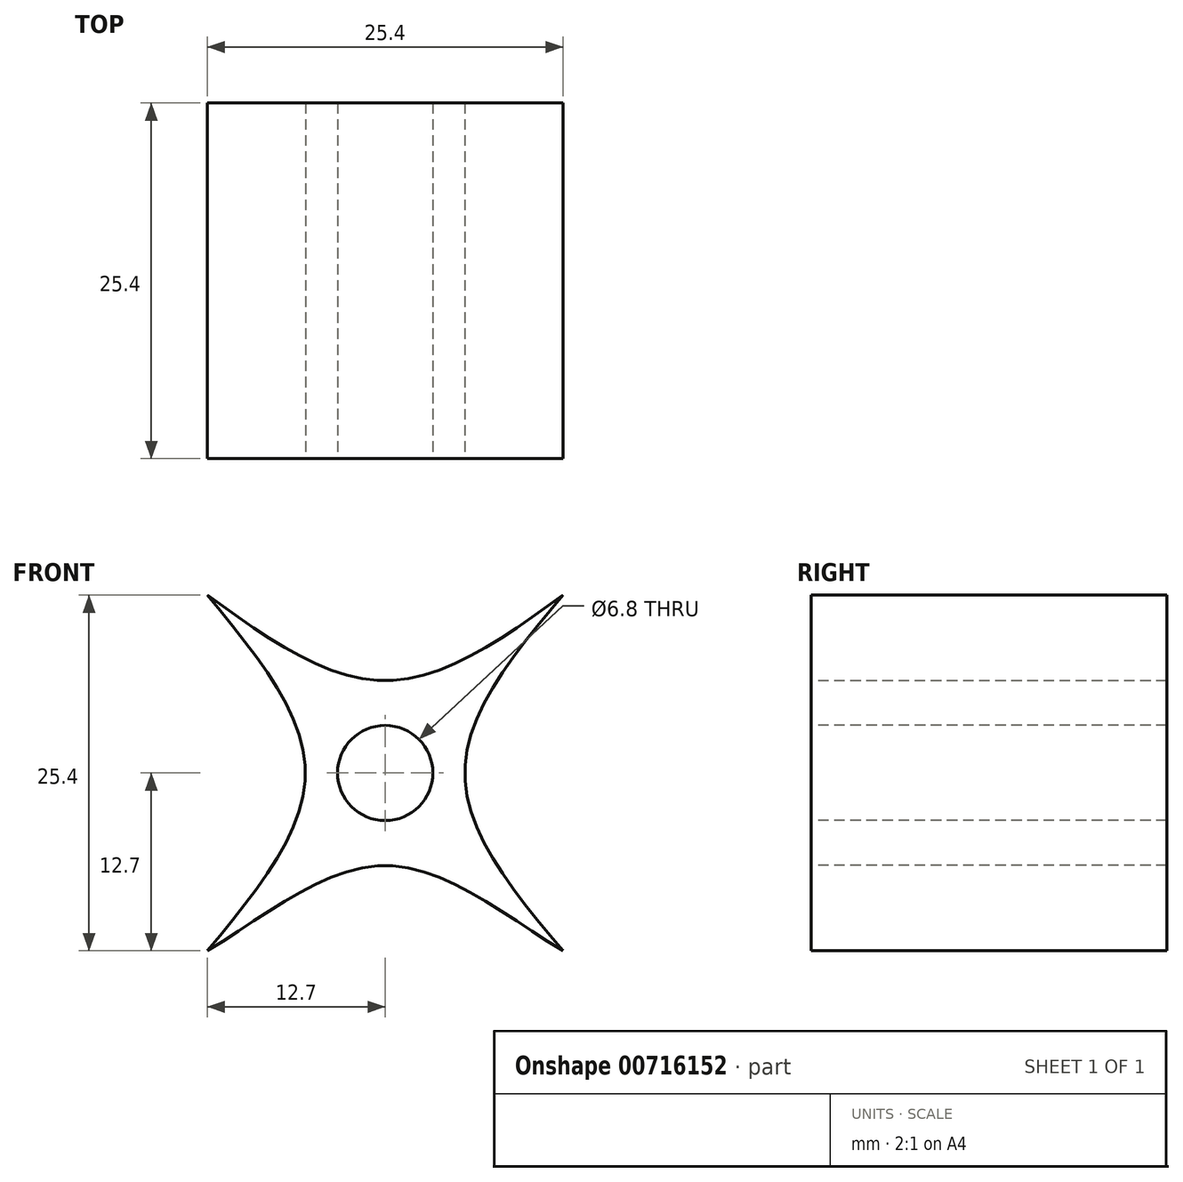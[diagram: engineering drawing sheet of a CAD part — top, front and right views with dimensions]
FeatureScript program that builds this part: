
annotation { "Feature Type Name" : "Feature", "Feature Type Description" : "" }
export const myFeature = defineFeature(function(context is Context, id is Id, definition is map)
    precondition{}
    {
        {
            var Q0;
            Q0=qCreatedBy(makeId("Front.planeOp"),FACE);
            var sketch = newSketch(context, id + "F0", { "sketchPlane" : qUnion([Q0])});
            skLineSegment(sketch, "E0.bottom", {"start": v(12.7, 12.7) * mm, "end": v(-12.7, 12.7) * mm});
            skLineSegment(sketch, "E0.top", {"start": v(12.7, -12.7) * mm, "end": v(-12.7, -12.7) * mm});
            skLineSegment(sketch, "E0.left", {"start": v(12.7, 12.7) * mm, "end": v(12.7, -12.7) * mm});
            skLineSegment(sketch, "E0.right", {"start": v(-12.7, 12.7) * mm, "end": v(-12.7, -12.7) * mm});
            skPoint(sketch, "E0.middle", {"position": v(0, 0) * mm});
            skSolve(sketch);
        }
        {
            var Q0;
            Q0 = qSketchRegion(id + "F0", true);
            extrude(context, id + "F1", {"entities" : qUnion([Q0]), "depth" : 25.4 * mm, "offsetDistance" : 25.4 * mm});
        }
        {
            var Q0;
            Q0=makeQuery(id+"F1.opExtrude","CAP_FACE",FACE,{"disambiguationData":[OSD([sQuery(id+"F0.wireOp",EDGE,"E0.bottom"),sQuery(id+"F0.wireOp",EDGE,"E0.top"),sQuery(id+"F0.wireOp",EDGE,"E0.left"),sQuery(id+"F0.wireOp",EDGE,"E0.right")])],"isStart":false});
            var sketch = newSketch(context, id + "F2", { "sketchPlane" : qUnion([Q0])});
            skFitSpline(sketch, "E1", {"points": [v(-12.7, 12.7) * mm, v(-5.69, 0) * mm, v(-12.7, -12.7) * mm], "startDerivative": vector(21.03, -25.4) * mm, "endDerivative": vector(-21.03, -25.4) * mm});
            skFitSpline(sketch, "E2", {"points": [v(-12.7, 12.7) * mm, v(0, 6.6) * mm, v(12.7, 12.7) * mm], "startDerivative": vector(25.4, -18.32) * mm, "endDerivative": vector(25.4, 18.32) * mm});
            skFitSpline(sketch, "E3", {"points": [v(12.7, 12.7) * mm, v(5.69, 0) * mm, v(12.7, -12.7) * mm], "startDerivative": vector(-21.63, -25.4) * mm, "endDerivative": vector(21.63, -25.4) * mm});
            skFitSpline(sketch, "E4", {"points": [v(-12.7, -12.7) * mm, v(0, -6.6) * mm, v(12.7, -12.7) * mm], "startDerivative": vector(25.4, 15.47) * mm, "endDerivative": vector(25.4, -15.47) * mm});
            skSolve(sketch);
        }
        {
            var Q0;
            Q0=makeQuery(id+"F2.imprint","IMPRINT",FACE,{"disambiguationData":[TD([[makeQuery(id+"F2.imprint","IMPRINT",EDGE,{"derivedFrom":sQuery(id+"F2.wireOp",EDGE,"E1")}),-1.0]])]});
            extrude(context, id + "F3", {"entities" : qUnion([Q0]), "operationType" : NewBodyOperationType.REMOVE, "endBound" : BoundingType.THROUGH_ALL, "oppositeDirection" : true, "depth" : 25.4 * mm, "offsetDistance" : 25.4 * mm});
        }
        {
            var Q0;
            Q0=makeQuery(id+"F2.imprint","IMPRINT",FACE,{"disambiguationData":[TD([[makeQuery(id+"F2.imprint","IMPRINT",EDGE,{"derivedFrom":sQuery(id+"F2.wireOp",EDGE,"E2")}),1.0]])]});
            extrude(context, id + "F4", {"entities" : qUnion([Q0]), "operationType" : NewBodyOperationType.REMOVE, "endBound" : BoundingType.THROUGH_ALL, "oppositeDirection" : true, "depth" : 25.4 * mm, "offsetDistance" : 25.4 * mm});
        }
        {
            var Q0;
            Q0=makeQuery(id+"F2.imprint","IMPRINT",FACE,{"disambiguationData":[TD([[makeQuery(id+"F2.imprint","IMPRINT",EDGE,{"derivedFrom":sQuery(id+"F2.wireOp",EDGE,"E3")}),1.0]])]});
            extrude(context, id + "F5", {"entities" : qUnion([Q0]), "operationType" : NewBodyOperationType.REMOVE, "endBound" : BoundingType.THROUGH_ALL, "oppositeDirection" : true, "depth" : 25.4 * mm, "offsetDistance" : 25.4 * mm});
        }
        {
            var Q0;
            Q0=makeQuery(id+"F2.imprint","IMPRINT",FACE,{"disambiguationData":[TD([[makeQuery(id+"F2.imprint","IMPRINT",EDGE,{"derivedFrom":sQuery(id+"F2.wireOp",EDGE,"E4")}),-1.0]])]});
            extrude(context, id + "F6", {"entities" : qUnion([Q0]), "operationType" : NewBodyOperationType.REMOVE, "endBound" : BoundingType.THROUGH_ALL, "oppositeDirection" : true, "depth" : 25.4 * mm, "offsetDistance" : 25.4 * mm});
        }
        {
            var Q0;
            Q0=makeQuery(id+"F1.opExtrude","CAP_FACE",FACE,{"disambiguationData":[OSD([sQuery(id+"F0.wireOp",EDGE,"E0.bottom"),sQuery(id+"F0.wireOp",EDGE,"E0.top"),sQuery(id+"F0.wireOp",EDGE,"E0.left"),sQuery(id+"F0.wireOp",EDGE,"E0.right")])],"isStart":false});
            var sketch = newSketch(context, id + "F7", { "sketchPlane" : qUnion([Q0])});
            skCircle(sketch, "E5", {"center": v(0, 0) * mm, "radius": 3.4 * mm});
            skSolve(sketch);
        }
        {
            var Q0;
            Q0 = qSketchRegion(id + "F7", true);
            extrude(context, id + "F8", {"entities" : qUnion([Q0]), "operationType" : NewBodyOperationType.REMOVE, "endBound" : BoundingType.THROUGH_ALL, "oppositeDirection" : true, "depth" : 25.4 * mm, "offsetDistance" : 25.4 * mm});
        }
    });
